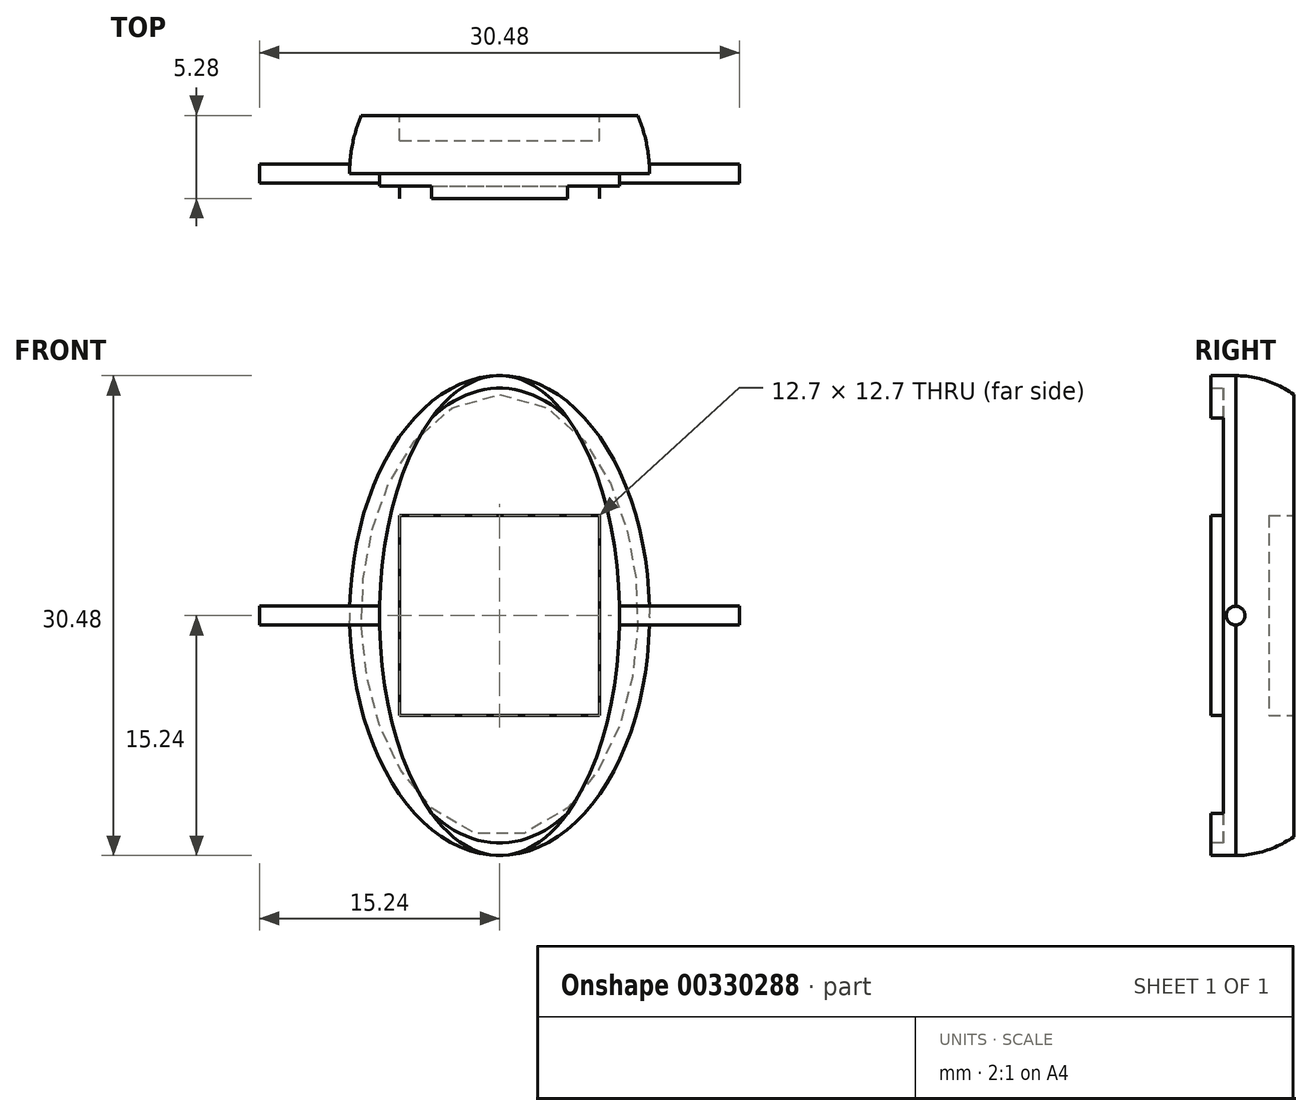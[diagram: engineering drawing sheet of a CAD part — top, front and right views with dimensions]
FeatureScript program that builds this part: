
annotation { "Feature Type Name" : "Feature", "Feature Type Description" : "" }
export const myFeature = defineFeature(function(context is Context, id is Id, definition is map)
    precondition{}
    {
        {
            var Q0;
            Q0=qCreatedBy(makeId("Front.planeOp"),FACE);
            var sketch = newSketch(context, id + "F0", { "sketchPlane" : qUnion([Q0])});
            skEllipticalArc(sketch, "E0", {});
            skLineSegment(sketch, "E1", {"start": v(0, 15.24) * mm, "end": v(0, -15.24) * mm});
            const initialGuessF0  = {"E0": [0, 0, 0, 1, 0.01524, 0.009525, 3.141592653589793, 0]};
            skSetInitialGuess(sketch, initialGuessF0);
            skSolve(sketch);
        }
        {
            var Q0;
            Q0=qSketchRegion(id+"F0",true);
            var Q1;
            Q1=sQuery(id+"F0.wireOp",EDGE,"E1");
            revolve(context, id + "F1", {"entities" : qUnion([Q0]), "axis" : qUnion([Q1]), "revolveType" : RevolveType.ONE_DIRECTION, "oppositeDirection" : true, "angle" : 180 * degree});
        }
        {
            var Q0;
            Q0=qCreatedBy(makeId("Right.planeOp"),FACE);
            var sketch = newSketch(context, id + "F2", { "sketchPlane" : qUnion([Q0])});
            skLineSegment(sketch, "E2.bottom", {"start": v(3.69, 15.9) * mm, "end": v(30.72, 15.9) * mm});
            skLineSegment(sketch, "E2.top", {"start": v(3.69, -22.6) * mm, "end": v(30.72, -22.6) * mm});
            skLineSegment(sketch, "E2.left", {"start": v(3.69, 15.9) * mm, "end": v(3.69, -22.6) * mm});
            skLineSegment(sketch, "E2.right", {"start": v(30.72, 15.9) * mm, "end": v(30.72, -22.6) * mm});
            skSolve(sketch);
        }
        {
            var Q0;
            Q0=qSketchRegion(id+"F2",true);
            extrude(context, id + "F3", {"entities" : qUnion([Q0]), "operationType" : NewBodyOperationType.REMOVE, "oppositeDirection" : true, "depth" : 25.4 * mm, "symmetric" : true});
        }
        {
            var Q0;
            Q0=qCreatedBy(makeId("Right.planeOp"),FACE);
            var sketch = newSketch(context, id + "F4", { "sketchPlane" : qUnion([Q0])});
            skCircle(sketch, "E3", {"center": v(0, 0) * mm, "radius": 0.6 * mm});
            skSolve(sketch);
        }
        {
            var Q0;
            Q0=makeQuery(id+"F1.opRevolve","CAP_FACE",FACE,{"disambiguationData":[OSD([sQuery(id+"F0.wireOp",EDGE,"E0"),sQuery(id+"F0.wireOp",EDGE,"E1")])],"isStart":false});
            var sketch = newSketch(context, id + "F5", { "sketchPlane" : qUnion([Q0])});
            skEllipticalArc(sketch, "E4.0", {});
            skEllipticalArc(sketch, "E4.1", {});
            const initialGuessF5  = {"E4.0": [0, 0, 0, 1, 0.01524, 0.00762, 0, 3.141592653589793], "E4.1": [0, 0, 0, 1, 0.01524, 0.00762, 3.141592653589793, 0]};
            skSetInitialGuess(sketch, initialGuessF5);
            skSolve(sketch);
        }
        {
            var Q0;
            Q0=qSketchRegion(id+"F5",true);
            extrude(context, id + "F6", {"entities" : qUnion([Q0]), "operationType" : NewBodyOperationType.ADD, "depth" : 1.59 * mm});
        }
        {
            var Q0;
            Q0=qSketchRegion(id+"F4",true);
            extrude(context, id + "F7", {"entities" : qUnion([Q0]), "operationType" : NewBodyOperationType.ADD, "depth" : 30.48 * mm, "symmetric" : true});
        }
        {
            var Q0;
            Q0=makeQuery(id+"F6.opExtrude","CAP_FACE",FACE,{"disambiguationData":[OSD([sQuery(id+"F5.wireOp",EDGE,"E4.0"),sQuery(id+"F5.wireOp",EDGE,"E4.1")])],"isStart":false});
            var sketch = newSketch(context, id + "F8", { "sketchPlane" : qUnion([Q0])});
            skEllipse(sketch, "E5", {"center": v(0, 0) * mm, "majorRadius": 14.45 * mm, "minorRadius": 8.73 * mm, "majorAxis": v(0, 1)});
            skSolve(sketch);
        }
        {
            var Q0;
            Q0=qSketchRegion(id+"F8",true);
            extrude(context, id + "F9", {"entities" : qUnion([Q0]), "operationType" : NewBodyOperationType.REMOVE, "oppositeDirection" : true, "depth" : 0.8 * mm});
        }
        {
            var Q0;
            Q0=makeQuery(id+"F9.boolean.opBoolean","COPY",FACE,{"derivedFrom":makeQuery(id+"F9.opExtrude","CAP_FACE",FACE,{"disambiguationData":[OSD([sQuery(id+"F8.wireOp",EDGE,"E5")])],"isStart":false})});
            var sketch = newSketch(context, id + "F10", { "sketchPlane" : qUnion([Q0])});
            skSolve(sketch);
        }
        {
            var Q0;
            Q0=makeQuery(id+"F10.imprint","IMPRINT",FACE,{"disambiguationData":[TD([[makeQuery(id+"F10.imprint","IMPRINT",EDGE,{"derivedFrom":makeQuery(id+"F9.boolean.opBoolean","COPY",EDGE,{"derivedFrom":makeQuery(id+"F9.opExtrude","CAP_EDGE",EDGE,{"disambiguationData":[OSD([sQuery(id+"F8.wireOp",EDGE,"E5")])],"isStart":false})})}),1.0]])]});
            var sketch = newSketch(context, id + "F11", { "sketchPlane" : qUnion([Q0])});
            skLineSegment(sketch, "E6.bottom", {"start": v(-6.35, 6.35) * mm, "end": v(6.35, 6.35) * mm});
            skLineSegment(sketch, "E6.top", {"start": v(-6.35, -6.35) * mm, "end": v(6.35, -6.35) * mm});
            skLineSegment(sketch, "E6.left", {"start": v(-6.35, 6.35) * mm, "end": v(-6.35, -6.35) * mm});
            skLineSegment(sketch, "E6.right", {"start": v(6.35, 6.35) * mm, "end": v(6.35, -6.35) * mm});
            skSolve(sketch);
        }
        {
            var Q0;
            Q0=qSketchRegion(id+"F11",true);
            extrude(context, id + "F12", {"entities" : qUnion([Q0]), "operationType" : NewBodyOperationType.ADD, "depth" : 0.8 * mm});
        }
        {
            var Q0;
            Q0=makeQuery(id+"F3.boolean.opBoolean","COPY",FACE,{"derivedFrom":makeQuery(id+"F3.opExtrude","SWEPT_FACE",FACE,{"disambiguationData":[OSD([sQuery(id+"F2.wireOp",EDGE,"E2.left")])]})});
            var sketch = newSketch(context, id + "F13", { "sketchPlane" : qUnion([Q0])});
            skLineSegment(sketch, "E7.0", {"start": v(6.35, 6.35) * mm, "end": v(-6.35, 6.35) * mm});
            skLineSegment(sketch, "E7.1", {"start": v(6.35, 6.35) * mm, "end": v(6.35, -6.35) * mm});
            skLineSegment(sketch, "E7.2", {"start": v(6.35, -6.35) * mm, "end": v(-6.35, -6.35) * mm});
            skLineSegment(sketch, "E7.3", {"start": v(-6.35, 6.35) * mm, "end": v(-6.35, -6.35) * mm});
            skSolve(sketch);
        }
        {
            var Q0;
            Q0=qSketchRegion(id+"F13",true);
            extrude(context, id + "F14", {"entities" : qUnion([Q0]), "operationType" : NewBodyOperationType.REMOVE, "oppositeDirection" : true, "depth" : 1.59 * mm});
        }
    });
